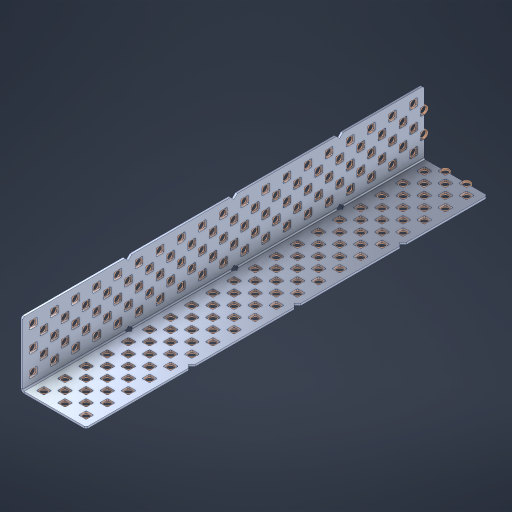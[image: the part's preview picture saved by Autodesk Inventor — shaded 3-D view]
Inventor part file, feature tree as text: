
AUTODESK INVENTOR PART (.ipt)
format: ipt  version: 2023 (Build 270158000, 158)  size: 2,109,440 bytes
history: native  units: in
note: dims shown in document units (in); Inventor stores cm internally (conversion verified against a paired STEP export)
features: other x232, extrude x188, sheet_metal_op x8, sketch x7, pattern_linear x3, mirror x1, chamfer x1
ambient origin geometry x8: Origin, YZ Plane, XZ Plane, XY Plane, X Axis, Y Axis, Z Axis, Center Point
bodies: Solid1 (feature_tree), Body (feature_tree)
feature tree (440):
  other  "Table"
  other  "Steel Angle 3x3x35"
  other  "Steel Angle 3x3x34"
  other  "Steel Angle 3x3x33"
  other  "Steel Angle 3x3x32"
  other  "Steel Angle 3x3x31"
  other  "Steel Angle 3x3x30"
  other  "Steel Angle 3x3x29"
  other  "Steel Angle 3x3x28"
  other  "Steel Angle 3x3x27"
  other  "Steel Angle 3x3x26"
  other  "Steel Angle 3x3x25"
  other  "Steel Angle 3x3x24"
  other  "Steel Angle 3x3x23"
  other  "Steel Angle 3x3x22"
  other  "Steel Angle 3x3x21"
  other  "Steel Angle 3x3x20"
  other  "Steel Angle 3x3x19"
  other  "Steel Angle 3x3x18"
  other  "Steel Angle 3x3x17"
  other  "Steel Angle 3x3x16"
  other  "Steel Angle 3x3x15"
  other  "Steel Angle 3x3x14"
  other  "Steel Angle 3x3x13"
  other  "Steel Angle 3x3x12"
  other  "Steel Angle 3x3x11"
  other  "Steel Angle 3x3x10"
  other  "Steel Angle 3x3x9"
  other  "Steel Angle 3x3x8"
  other  "Steel Angle 3x3x7"
  other  "Steel Angle 3x3x6"
  other  "Steel Angle 3x3x5"
  other  "Steel Angle 3x3x4"
  other  "Steel Angle 3x3x3"
  other  "Steel Angle 3x3x2"
  other  "Steel Angle 3x3x1"
  sheet_metal_op  "Flanges"
  sheet_metal_op  "Body Pattern"
  pattern_linear  "Center Double"  Spacing1=1.5in  [1 undecoded]
  pattern_linear  "Center Pattern"  Spacing1=0.1875in  [1 undecoded]
  other  "Arc Length"
  pattern_linear  "Notch Pattern"  Spacing1=0.0469in  [1 undecoded]
  other  "Diagonal Plane"
  mirror  "Everything Mirrored"
  chamfer  "End Chamfer"
  sketch  "Sketch1"  dims[d0=1.5in]
  other  "Plate1"
  sketch  "Sketch2"  dims[d1=9.5in]
  other  "Plate2"
  sheet_metal_op  "Bend1"
  sheet_metal_op  "Corner1"
  sketch  "Sketch8"  dims[d2=0.0469in]
  sketch  "Sketch9"  dims[d3=0.0469in]
  other  "Srf91"
  sheet_metal_op  "Body Pattern Sketch"
  other  "Srf92"
  sketch  "Sketch13"  dims[d4=0.0234in]
  sketch  "Sketch15"  dims[d5=0.0938in]
  sketch  "Sketch16"  dims[d6=0.0469in d7=1.5in d8=90.0deg d9=0.0312in d10=0.1875in d11=0.0469in d12=0.0469in d49=0.182in d50=0.02in d52=0.25in d53=0.0469in d54=0.0in d55=0.172in d56=1.0in d57=0.0in d85=0.1473in d86=0.1659in d89=0.0469in d90=0.0in d91=0.04in d92=0.0491in d95=2.5in d96=0.04in d97=0.25in d98=45.0deg d106=0.182in d107=0.02in d110=0.0469in d111=0.0in d112=0.172in d113=0.5in d114=0.0in d117=0.5in d126=0.0491in d127=0.1227in d128=0.08in d129=0.04in d130=2.5in d131=0.25in d132=7.4803in d134=0.5in d135=1.1811in d137=0.5in d140=0.5in d141=1.0in d142=0.3937in d144=0.5in d145=0.071in d146=0.7874in d148=0.5in]
  other  "Srf786"
  other  "Srf856"
  other  "Srf889"
  other  "Srf890"
  other  "Srf891"
  other  "Srf1275"
  other  "Srf1276"
  other  "Srf1278"
  other  "Srf1277"
  other  "Srf1285"
  other  "Srf1286"
  other  "Srf1287"
  other  "Srf1445"
  other  "Srf1446"
  other  "Srf1447"
  other  "Srf1448"
  other  "Srf1449"
  other  "Srf1537"
  other  "Srf1538"
  other  "Srf1539"
  other  "Srf1540"
  other  "Srf1541"
  other  "Srf1807"
  other  "Srf1808"
  other  "Srf1809"
  other  "Srf1810"
  other  "Srf1811"
  other  "Srf1812"
  other  "Srf1813"
  other  "Srf1814"
  other  "Srf1815"
  other  "Srf1816"
  other  "Srf1959"
  other  "Srf1960"
  other  "Srf1961"
  other  "Srf1962"
  other  "Srf1963"
  other  "Srf1964"
  other  "Srf1965"
  other  "Srf1966"
  other  "Srf1967"
  other  "Srf1968"
  other  "Srf2009"
  other  "Srf2010"
  other  "Srf2011"
  other  "Srf2012"
  other  "Srf2013"
  other  "Srf2014"
  other  "Srf2015"
  other  "Srf2016"
  other  "Srf2017"
  other  "Srf2018"
  other  "Srf2019"
  other  "Srf2020"
  other  "Srf2021"
  other  "Srf2022"
  other  "Srf2023"
  other  "Srf2024"
  other  "Srf2025"
  other  "Srf2026"
  other  "Srf2027"
  other  "Srf2043"
  other  "Srf2044"
  other  "Srf2045"
  other  "Srf2046"
  other  "Srf2047"
  other  "Srf2048"
  other  "Srf2049"
  other  "Srf2050"
  other  "Srf2051"
  other  "Srf2052"
  other  "Srf2053"
  other  "Srf2054"
  other  "Srf2055"
  other  "Srf2056"
  other  "Srf2057"
  other  "Srf2058"
  other  "Srf2059"
  other  "Srf2060"
  other  "Srf2076"
  other  "Srf2077"
  other  "Srf2078"
  other  "Srf2079"
  other  "Srf2080"
  other  "Srf2081"
  other  "Srf2082"
  other  "Srf2083"
  other  "Srf2084"
  other  "Srf2085"
  other  "Srf2086"
  other  "Srf2087"
  other  "Srf2088"
  other  "Srf2089"
  other  "Srf2090"
  other  "Srf2091"
  other  "Srf2092"
  other  "Srf2093"
  other  "Srf2094"
  other  "Srf2095"
  other  "Srf2096"
  other  "Srf2097"
  other  "Srf2098"
  other  "Srf2099"
  other  "Srf2100"
  other  "Srf2101"
  other  "Srf2102"
  other  "Srf2103"
  other  "Srf2104"
  other  "Srf2105"
  other  "Srf2106"
  other  "Srf2107"
  other  "Srf2108"
  other  "Srf2109"
  other  "Srf2110"
  other  "Srf2111"
  other  "Srf2112"
  other  "Srf2113"
  other  "Srf2114"
  other  "Srf2115"
  other  "Srf2116"
  other  "Srf2117"
  other  "Srf2118"
  other  "Srf2119"
  other  "Srf2120"
  other  "Srf2121"
  other  "Srf2122"
  other  "Srf2123"
  other  "Srf2124"
  other  "Srf2125"
  other  "Srf2126"
  other  "Srf2127"
  other  "Srf2128"
  other  "Srf2129"
  other  "Srf2130"
  other  "Srf2179"
  other  "Srf2180"
  other  "Srf2181"
  other  "Srf2182"
  other  "Srf2183"
  other  "Srf2184"
  other  "Srf2185"
  other  "Srf2186"
  other  "Srf2187"
  other  "Srf2188"
  other  "Srf2189"
  other  "Srf2190"
  other  "Srf2191"
  other  "Srf2192"
  other  "Srf2193"
  other  "Srf2194"
  other  "Srf2195"
  other  "Srf2196"
  other  "Srf2197"
  other  "Srf2198"
  other  "Srf2199"
  other  "Srf2200"
  other  "Srf2201"
  other  "Srf2202"
  other  "Srf2203"
  other  "Srf2204"
  other  "Srf2205"
  other  "Srf2206"
  other  "Srf2207"
  other  "Srf2208"
  other  "Srf2209"
  other  "Srf2210"
  other  "Srf2211"
  other  "Srf2212"
  other  "Srf2213"
  other  "Srf2214"
  other  "Srf2215"
  other  "Srf2216"
  other  "Srf2217"
  other  "Srf2218"
  other  "Srf2219"
  other  "Srf2220"
  other  "Srf2221"
  other  "Srf2222"
  other  "Srf2223"
  other  "Srf2224"
  other  "Srf2225"
  other  "Srf2226"
  other  "Srf2227"
  other  "Srf2228"
  other  "Srf2229"
  other  "Srf2230"
  other  "Srf2231"
  other  "Srf2232"
  sheet_metal_op  "Body Stamp"
  sheet_metal_op  "Body Circle"
  other  "Center Stamp"
  other  "Center Circle"
  sheet_metal_op  "Notch"
  extrude  "ExtrusionSrf92"  Depth=0.0469in
  extrude  "ExtrusionSrf856"  Depth=0.182in
  extrude  "ExtrusionSrf889"  Depth=0.02in
  extrude  "ExtrusionSrf890"  Depth=0.25in
  extrude  "ExtrusionSrf891"  Depth=0.0469in
  extrude  "ExtrusionSrf1275"  TaperAngle=0.0deg  [1 undecoded]
  extrude  "ExtrusionSrf1276"  Depth=0.5in
  extrude  "ExtrusionSrf1277"  Depth=1.0in TaperAngle=0.0deg
  extrude  "ExtrusionSrf1345"  Depth=0.5in
  extrude  "ExtrusionSrf1346"  Depth=0.5in
  extrude  "ExtrusionSrf1347"  Depth=0.0469in
  extrude  "ExtrusionSrf1348"  Depth=0.5in TaperAngle=0.0deg
  extrude  "ExtrusionSrf1445"  Depth=0.5in
  extrude  "ExtrusionSrf1446"  Depth=0.25in TaperAngle=45.0deg
  extrude  "ExtrusionSrf1447"  Depth=0.182in
  extrude  "ExtrusionSrf1448"  Depth=0.02in
  extrude  "ExtrusionSrf1449"  Depth=0.0469in
  extrude  "ExtrusionSrf1537"  TaperAngle=0.0deg  [1 undecoded]
  extrude  "ExtrusionSrf1538"  Depth=0.5in
  extrude  "ExtrusionSrf1539"  Depth=0.5in TaperAngle=0.0deg
  extrude  "ExtrusionSrf1540"  Depth=0.5in
  extrude  "ExtrusionSrf1541"  Depth=0.5in
  extrude  "ExtrusionSrf1807"  Depth=0.5in
  extrude  "ExtrusionSrf1808"  Depth=0.5in
  extrude  "ExtrusionSrf1809"  Depth=0.5in
  extrude  "ExtrusionSrf1810"  Depth=0.5in
  extrude  "ExtrusionSrf1811"  Depth=0.25in
  extrude  "ExtrusionSrf1812"  Depth=0.5in
  extrude  "ExtrusionSrf1813"  Depth=0.5in
  extrude  "ExtrusionSrf1814"  Depth=0.5in
  extrude  "ExtrusionSrf1815"  Depth=1.0in
  extrude  "ExtrusionSrf1816"  Depth=0.3937in
  extrude  "ExtrusionSrf1959"  Depth=0.5in
  extrude  "ExtrusionSrf1960"  Depth=0.5in
  extrude  "ExtrusionSrf1961"  [1 undecoded]
  extrude  "ExtrusionSrf1962"  [1 undecoded]
  extrude  "ExtrusionSrf1963"  [1 undecoded]
  extrude  "ExtrusionSrf1964"  [1 undecoded]
  extrude  "ExtrusionSrf1965"  [1 undecoded]
  extrude  "ExtrusionSrf1966"  [1 undecoded]
  extrude  "ExtrusionSrf1967"  [1 undecoded]
  extrude  "ExtrusionSrf1968"  [1 undecoded]
  extrude  "ExtrusionSrf2009"  [1 undecoded]
  extrude  "ExtrusionSrf2010"  [1 undecoded]
  extrude  "ExtrusionSrf2011"  [1 undecoded]
  extrude  "ExtrusionSrf2012"  [1 undecoded]
  extrude  "ExtrusionSrf2013"  [1 undecoded]
  extrude  "ExtrusionSrf2014"  [1 undecoded]
  extrude  "ExtrusionSrf2015"  [1 undecoded]
  extrude  "ExtrusionSrf2016"  [1 undecoded]
  extrude  "ExtrusionSrf2017"  [1 undecoded]
  extrude  "ExtrusionSrf2018"  [1 undecoded]
  extrude  "ExtrusionSrf2019"  [1 undecoded]
  extrude  "ExtrusionSrf2020"  [1 undecoded]
  extrude  "ExtrusionSrf2021"  [1 undecoded]
  extrude  "ExtrusionSrf2022"  [1 undecoded]
  extrude  "ExtrusionSrf2023"  [1 undecoded]
  extrude  "ExtrusionSrf2024"  [1 undecoded]
  extrude  "ExtrusionSrf2025"  [1 undecoded]
  extrude  "ExtrusionSrf2026"  [1 undecoded]
  extrude  "ExtrusionSrf2027"  [1 undecoded]
  extrude  "ExtrusionSrf2043"  [1 undecoded]
  extrude  "ExtrusionSrf2044"  [1 undecoded]
  extrude  "ExtrusionSrf2045"  [1 undecoded]
  extrude  "ExtrusionSrf2046"  [1 undecoded]
  extrude  "ExtrusionSrf2047"  [1 undecoded]
  extrude  "ExtrusionSrf2048"  [1 undecoded]
  extrude  "ExtrusionSrf2049"  [1 undecoded]
  extrude  "ExtrusionSrf2050"  [1 undecoded]
  extrude  "ExtrusionSrf2051"  [1 undecoded]
  extrude  "ExtrusionSrf2052"  [1 undecoded]
  extrude  "ExtrusionSrf2053"  [1 undecoded]
  extrude  "ExtrusionSrf2054"  [1 undecoded]
  extrude  "ExtrusionSrf2055"  [1 undecoded]
  extrude  "ExtrusionSrf2056"  [1 undecoded]
  extrude  "ExtrusionSrf2057"  [1 undecoded]
  extrude  "ExtrusionSrf2058"  [1 undecoded]
  extrude  "ExtrusionSrf2059"  [1 undecoded]
  extrude  "ExtrusionSrf2060"  [1 undecoded]
  extrude  "ExtrusionSrf2076"  [1 undecoded]
  extrude  "ExtrusionSrf2077"  [1 undecoded]
  extrude  "ExtrusionSrf2078"  [1 undecoded]
  extrude  "ExtrusionSrf2079"  [1 undecoded]
  extrude  "ExtrusionSrf2080"  [1 undecoded]
  extrude  "ExtrusionSrf2081"  [1 undecoded]
  extrude  "ExtrusionSrf2082"  [1 undecoded]
  extrude  "ExtrusionSrf2083"  [1 undecoded]
  extrude  "ExtrusionSrf2084"  [1 undecoded]
  extrude  "ExtrusionSrf2085"  [1 undecoded]
  extrude  "ExtrusionSrf2086"  [1 undecoded]
  extrude  "ExtrusionSrf2087"  [1 undecoded]
  extrude  "ExtrusionSrf2088"  [1 undecoded]
  extrude  "ExtrusionSrf2089"  [1 undecoded]
  extrude  "ExtrusionSrf2090"  [1 undecoded]
  extrude  "ExtrusionSrf2091"  [1 undecoded]
  extrude  "ExtrusionSrf2092"  [1 undecoded]
  extrude  "ExtrusionSrf2093"  [1 undecoded]
  extrude  "ExtrusionSrf2094"  [1 undecoded]
  extrude  "ExtrusionSrf2095"  [1 undecoded]
  extrude  "ExtrusionSrf2096"  [1 undecoded]
  extrude  "ExtrusionSrf2097"  [1 undecoded]
  extrude  "ExtrusionSrf2098"  [1 undecoded]
  extrude  "ExtrusionSrf2099"  [1 undecoded]
  extrude  "ExtrusionSrf2100"  [1 undecoded]
  extrude  "ExtrusionSrf2101"  [1 undecoded]
  extrude  "ExtrusionSrf2102"  [1 undecoded]
  extrude  "ExtrusionSrf2103"  [1 undecoded]
  extrude  "ExtrusionSrf2104"  [1 undecoded]
  extrude  "ExtrusionSrf2105"  [1 undecoded]
  extrude  "ExtrusionSrf2106"  [1 undecoded]
  extrude  "ExtrusionSrf2107"  [1 undecoded]
  extrude  "ExtrusionSrf2108"  [1 undecoded]
  extrude  "ExtrusionSrf2109"  [1 undecoded]
  extrude  "ExtrusionSrf2110"  [1 undecoded]
  extrude  "ExtrusionSrf2111"  [1 undecoded]
  extrude  "ExtrusionSrf2112"  [1 undecoded]
  extrude  "ExtrusionSrf2113"  [1 undecoded]
  extrude  "ExtrusionSrf2114"  [1 undecoded]
  extrude  "ExtrusionSrf2115"  [1 undecoded]
  extrude  "ExtrusionSrf2116"  [1 undecoded]
  extrude  "ExtrusionSrf2117"  [1 undecoded]
  extrude  "ExtrusionSrf2118"  [1 undecoded]
  extrude  "ExtrusionSrf2119"  [1 undecoded]
  extrude  "ExtrusionSrf2120"  [1 undecoded]
  extrude  "ExtrusionSrf2121"  [1 undecoded]
  extrude  "ExtrusionSrf2122"  [1 undecoded]
  extrude  "ExtrusionSrf2123"  [1 undecoded]
  extrude  "ExtrusionSrf2124"  [1 undecoded]
  extrude  "ExtrusionSrf2125"  [1 undecoded]
  extrude  "ExtrusionSrf2126"  [1 undecoded]
  extrude  "ExtrusionSrf2127"  [1 undecoded]
  extrude  "ExtrusionSrf2128"  [1 undecoded]
  extrude  "ExtrusionSrf2129"  [1 undecoded]
  extrude  "ExtrusionSrf2130"  [1 undecoded]
  extrude  "ExtrusionSrf2179"  [1 undecoded]
  extrude  "ExtrusionSrf2180"  [1 undecoded]
  extrude  "ExtrusionSrf2181"  [1 undecoded]
  extrude  "ExtrusionSrf2182"  [1 undecoded]
  extrude  "ExtrusionSrf2183"  [1 undecoded]
  extrude  "ExtrusionSrf2184"  [1 undecoded]
  extrude  "ExtrusionSrf2185"  [1 undecoded]
  extrude  "ExtrusionSrf2186"  [1 undecoded]
  extrude  "ExtrusionSrf2187"  [1 undecoded]
  extrude  "ExtrusionSrf2188"  [1 undecoded]
  extrude  "ExtrusionSrf2189"  [1 undecoded]
  extrude  "ExtrusionSrf2190"  [1 undecoded]
  extrude  "ExtrusionSrf2191"  [1 undecoded]
  extrude  "ExtrusionSrf2192"  [1 undecoded]
  extrude  "ExtrusionSrf2193"  [1 undecoded]
  extrude  "ExtrusionSrf2194"  [1 undecoded]
  extrude  "ExtrusionSrf2195"  [1 undecoded]
  extrude  "ExtrusionSrf2196"  [1 undecoded]
  extrude  "ExtrusionSrf2197"  [1 undecoded]
  extrude  "ExtrusionSrf2198"  [1 undecoded]
  extrude  "ExtrusionSrf2199"  [1 undecoded]
  extrude  "ExtrusionSrf2200"  [1 undecoded]
  extrude  "ExtrusionSrf2201"  [1 undecoded]
  extrude  "ExtrusionSrf2202"  [1 undecoded]
  extrude  "ExtrusionSrf2203"  [1 undecoded]
  extrude  "ExtrusionSrf2204"  [1 undecoded]
  extrude  "ExtrusionSrf2205"  [1 undecoded]
  extrude  "ExtrusionSrf2206"  [1 undecoded]
  extrude  "ExtrusionSrf2207"  [1 undecoded]
  extrude  "ExtrusionSrf2208"  [1 undecoded]
  extrude  "ExtrusionSrf2209"  [1 undecoded]
  extrude  "ExtrusionSrf2210"  [1 undecoded]
  extrude  "ExtrusionSrf2211"  [1 undecoded]
  extrude  "ExtrusionSrf2212"  [1 undecoded]
  extrude  "ExtrusionSrf2213"  [1 undecoded]
  extrude  "ExtrusionSrf2214"  [1 undecoded]
  extrude  "ExtrusionSrf2215"  [1 undecoded]
  extrude  "ExtrusionSrf2216"  [1 undecoded]
  extrude  "ExtrusionSrf2217"  [1 undecoded]
  extrude  "ExtrusionSrf2218"  [1 undecoded]
  extrude  "ExtrusionSrf2219"  [1 undecoded]
  extrude  "ExtrusionSrf2220"  [1 undecoded]
  extrude  "ExtrusionSrf2221"  [1 undecoded]
  extrude  "ExtrusionSrf2222"  [1 undecoded]
  extrude  "ExtrusionSrf2223"  [1 undecoded]
  extrude  "ExtrusionSrf2224"  [1 undecoded]
  extrude  "ExtrusionSrf2225"  [1 undecoded]
  extrude  "ExtrusionSrf2226"  [1 undecoded]
  extrude  "ExtrusionSrf2227"  [1 undecoded]
  extrude  "ExtrusionSrf2228"  [1 undecoded]
  extrude  "ExtrusionSrf2229"  [1 undecoded]
  extrude  "ExtrusionSrf2230"  [1 undecoded]
  extrude  "ExtrusionSrf2231"  [1 undecoded]
  extrude  "ExtrusionSrf2232"  [1 undecoded]
note: 159 required parameter values undecoded (feature->parameter linkage not recoverable at this tier; creation-order binding heuristic only, values carry confidence <= 0.55)
